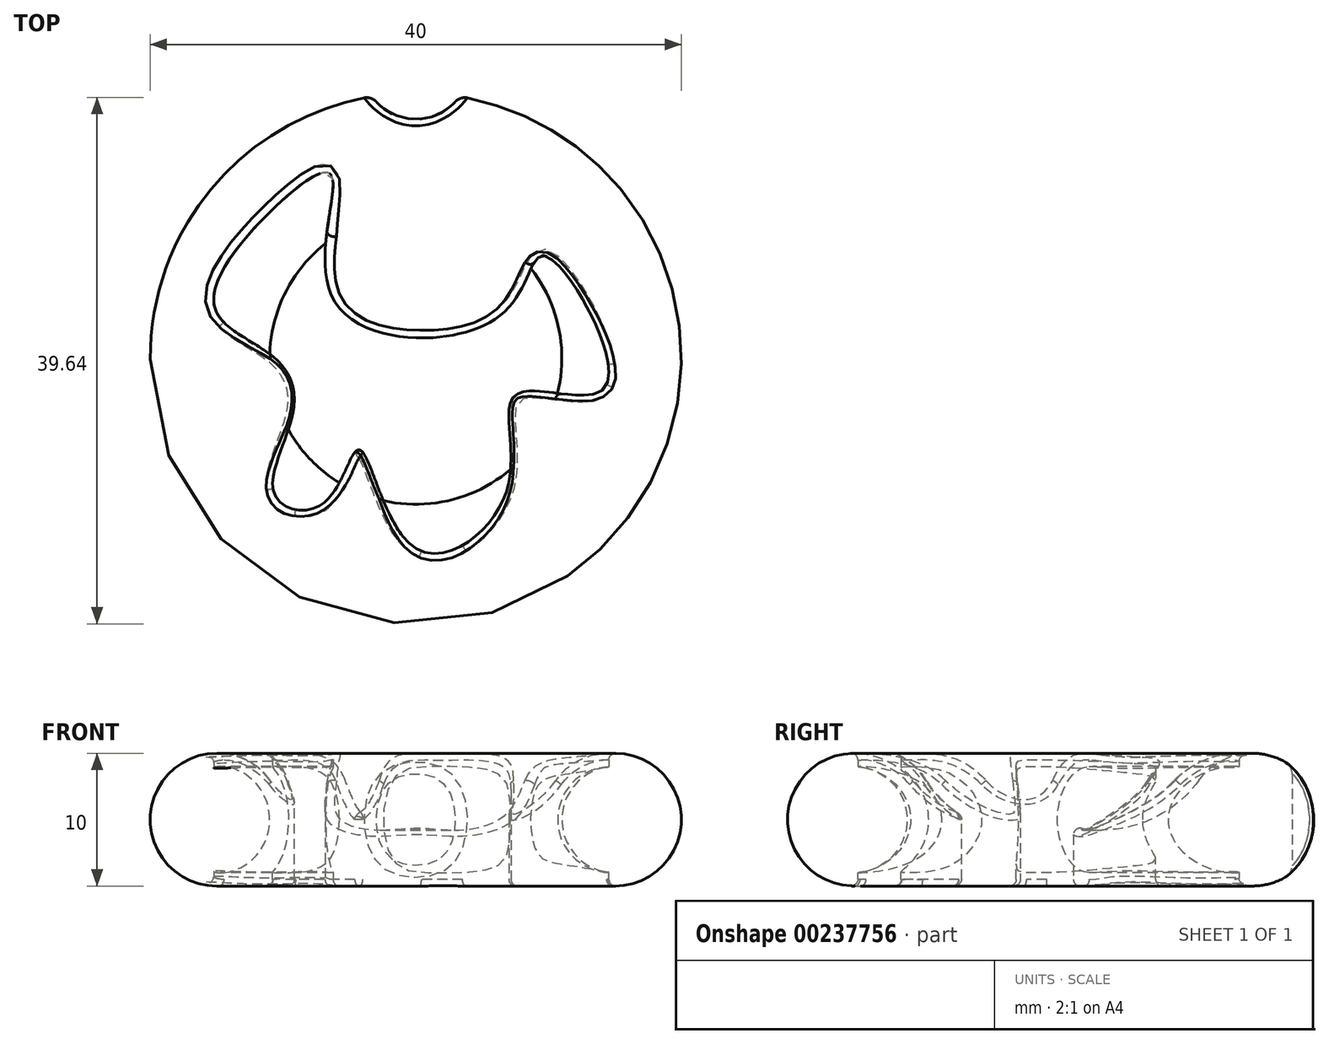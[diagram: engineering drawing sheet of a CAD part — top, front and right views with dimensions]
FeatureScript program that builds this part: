
annotation { "Feature Type Name" : "Feature", "Feature Type Description" : "" }
export const myFeature = defineFeature(function(context is Context, id is Id, definition is map)
    precondition{}
    {
        {
            var Q0;
            Q0=qCreatedBy(makeId("Front.planeOp"),FACE);
            var sketch = newSketch(context, id + "F0", { "sketchPlane" : qUnion([Q0])});
            skArc(sketch, "E0", {"start": v(-10.95, 7.94) * mm, "mid": v(-6, 4.53) * mm, "end": v(0, 5) * mm});
            skArc(sketch, "E1", {"start": v(-10.95, 7.94) * mm, "mid": v(-19.45, 7.27) * mm, "end": v(-15, 0) * mm});
            skLineSegment(sketch, "E2", {"start": v(-15, 0) * mm, "end": v(0, 0) * mm});
            skLineSegment(sketch, "E3", {"start": v(0, 0) * mm, "end": v(0, 5) * mm});
            skPoint(sketch, "E4.orphan", {"position": v(-17.04, 0) * mm});
            skSolve(sketch);
        }
        {
            var Q0;
            Q0=makeQuery(id+"F0.imprint","IMPRINT",FACE,{"disambiguationData":[TD([[makeQuery(id+"F0.imprint","IMPRINT",EDGE,{"derivedFrom":sQuery(id+"F0.wireOp",EDGE,"E0")}),-1.0]])]});
            var Q1;
            Q1=sQuery(id+"F0.wireOp",EDGE,"E3");
            revolve(context, id + "F1", {"entities" : qUnion([Q0]), "axis" : qUnion([Q1]), "revolveType" : RevolveType.FULL});
        }
        {
            var Q0;
            Q0=qCreatedBy(makeId("Top.planeOp"),FACE);
            cPlane(context, id + "F2", {"entities" : qUnion([Q0]), "cplaneType" : CPlaneType.OFFSET, "offset" : 10 * mm, "width" : 150 * mm, "height" : 150 * mm});
        }
        {
            var Q0;
            Q0=qCreatedBy(id+"F2.planeOp",FACE);
            var sketch = newSketch(context, id + "F3", { "sketchPlane" : qUnion([Q0])});
            skFitSpline(sketch, "E5", {"points": [v(-15.11, 3.71) * mm, v(-11.13, 10.87) * mm, v(-6.36, 13.79) * mm, v(-6.1, 4.24) * mm, v(6.63, 3.45) * mm, v(9.8, 7.69) * mm, v(14.32, -2.12) * mm, v(7.69, -2.65) * mm, v(6.9, -9.8) * mm, v(0, -14.32) * mm, v(-4.24, -6.9) * mm, v(-6.9, -10.87) * mm, v(-10.6, -10.34) * mm, v(-9.28, -4.24) * mm, v(-10.6, 0) * mm, v(-15.11, 3.71) * mm]});
            skSolve(sketch);
        }
        {
            var Q0;
            Q0 = qSketchRegion(id + "F3", true);
            extrude(context, id + "F4", {"entities" : qUnion([Q0]), "operationType" : NewBodyOperationType.REMOVE, "endBound" : BoundingType.THROUGH_ALL, "oppositeDirection" : true, "depth" : 25 * mm});
        }
        {
            var Q0;
            Q0=qCreatedBy(makeId("Front.planeOp"),FACE);
            var sketch = newSketch(context, id + "F5", { "sketchPlane" : qUnion([Q0])});
            skCircle(sketch, "E6", {"center": v(-15, 5) * mm, "radius": 4 * mm});
            skSolve(sketch);
        }
        {
            var Q0;
            Q0 = qSketchRegion(id + "F5", true);
            var Q1;
            Q1=sQuery(id+"F0.wireOp",EDGE,"E3");
            revolve(context, id + "F6", {"operationType" : NewBodyOperationType.ADD, "entities" : qUnion([Q0]), "axis" : qUnion([Q1]), "revolveType" : RevolveType.FULL});
        }
        {
            var Q0;
            Q0=qCreatedBy(makeId("Top.planeOp"),FACE);
            var sketch = newSketch(context, id + "F7", { "sketchPlane" : qUnion([Q0])});
            skCircle(sketch, "E7", {"center": v(0, 22) * mm, "radius": 4 * mm});
            skSolve(sketch);
        }
        {
            var Q0;
            Q0=makeQuery(id+"F7.imprint","IMPRINT",FACE,{"disambiguationData":[TD([[makeQuery(id+"F7.imprint","IMPRINT",EDGE,{"derivedFrom":sQuery(id+"F7.wireOp",EDGE,"E7")}),1.0]])]});
            extrude(context, id + "F8", {"entities" : qUnion([Q0]), "operationType" : NewBodyOperationType.REMOVE, "oppositeDirection" : true, "depth" : 25 * mm});
        }
        {
            var Q0;
            Q0=makeQuery(id+"F7.imprint","IMPRINT",FACE,{"disambiguationData":[TD([[makeQuery(id+"F7.imprint","IMPRINT",EDGE,{"derivedFrom":sQuery(id+"F7.wireOp",EDGE,"E7")}),1.0]])]});
            extrude(context, id + "F9", {"entities" : qUnion([Q0]), "operationType" : NewBodyOperationType.REMOVE, "oppositeDirection" : true, "depth" : 25 * mm});
        }
        {
            var Q0;
            Q0=makeQuery(id+"F7.imprint","IMPRINT",FACE,{"disambiguationData":[TD([[makeQuery(id+"F7.imprint","IMPRINT",EDGE,{"derivedFrom":sQuery(id+"F7.wireOp",EDGE,"E7")}),1.0]])]});
            extrude(context, id + "F10", {"entities" : qUnion([Q0]), "operationType" : NewBodyOperationType.REMOVE, "depth" : 34.3 * mm});
        }
        {
            var Q0;
            Q0=makeQuery(id+"F10.boolean.opBoolean","INTERSECT",EDGE,{"derivedFrom":[makeQuery(id+"F1.opRevolve","SWEPT_FACE",FACE,{"disambiguationData":[OSD([sQuery(id+"F0.wireOp",EDGE,"E1")])]}),makeQuery(id+"F10.opExtrude","SWEPT_FACE",FACE,{"disambiguationData":[OSD([sQuery(id+"F7.wireOp",EDGE,"E7")])]})]});
            fillet(context, id + "F11", {"entities" : qUnion([Q0]), "radius" : 1 * mm, "tangentPropagation" : true, "allowEdgeOverflow" : false});
        }
        {
            var Q0;
            Q0=makeQuery(id+"F4.boolean.opBoolean","INTERSECT",EDGE,{"derivedFrom":[makeQuery(id+"F1.opRevolve","SWEPT_FACE",FACE,{"disambiguationData":[OSD([sQuery(id+"F0.wireOp",EDGE,"E2")])]}),makeQuery(id+"F4.opExtrude","SWEPT_FACE",FACE,{"disambiguationData":[OSD([sQuery(id+"F3.wireOp",EDGE,"E5")])]})]});
            var Q1;
            Q1=makeQuery(id+"F4.boolean.opBoolean","INTERSECT",EDGE,{"disambiguationData":[OD(1.0)],"derivedFrom":[makeQuery(id+"F1.opRevolve","SWEPT_FACE",FACE,{"disambiguationData":[OSD([sQuery(id+"F0.wireOp",EDGE,"E1")])]}),makeQuery(id+"F4.opExtrude","SWEPT_FACE",FACE,{"disambiguationData":[OSD([sQuery(id+"F3.wireOp",EDGE,"E5")])]})]});
            fillet(context, id + "F12", {"entities" : qUnion([Q0, Q1]), "radius" : 0.5 * mm, "tangentPropagation" : true, "allowEdgeOverflow" : false});
        }
    });
